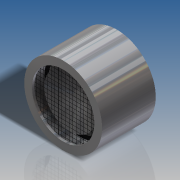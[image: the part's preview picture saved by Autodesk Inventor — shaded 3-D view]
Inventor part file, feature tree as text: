
AUTODESK INVENTOR PART (.ipt)
format: ipt  version: 2016 SP2 (Build 200236200, 236)  size: 694,784 bytes
history: native  units: in
note: dims shown in document units (in); Inventor stores cm internally (conversion verified against a paired STEP export)
features: sketch x2, revolve x2, extrude x2, pattern_circular x1
ambient origin geometry x8: Origin, YZ Plane, XZ Plane, XY Plane, X Axis, Y Axis, Z Axis, Center Point
bodies: Solid1 (feature_tree), Solid2 (feature_tree), Solid3 (feature_tree)
feature tree (7):
  sketch  "Sketch2"  dims[d0=0.5039in d1=0.3471in]
  revolve  "Revolution1"  [1 undecoded]
  revolve  "Revolution2"  [1 undecoded]
  extrude  "Extrusion2"  Depth=0.3937in
  extrude  "Extrusion3"  Depth=0.3937in
  pattern_circular  "Circular Pattern1"  [2 undecoded]
  sketch  "Sketch3"  dims[d2=0.0151in d3=0.4031in d4=0.1056in d5=0.0315in d6=0.3359in d7=0.0in d8=0.0604in d9=1.0706in d10=90.0deg d11=90.0deg d12=0.0016in d15=0.4535in d16=0.0in d17=3.5433in d19=0.0236in d20=0.3937in d22=0.3937in d24=3.5433in d26=0.0236in d27=0.3937in d29=0.3937in d31=0.7874in d32=90.0deg d34=0.3937in d35=0.0in]
note: 4 required parameter values undecoded (feature->parameter linkage not recoverable at this tier; creation-order binding heuristic only, values carry confidence <= 0.55)